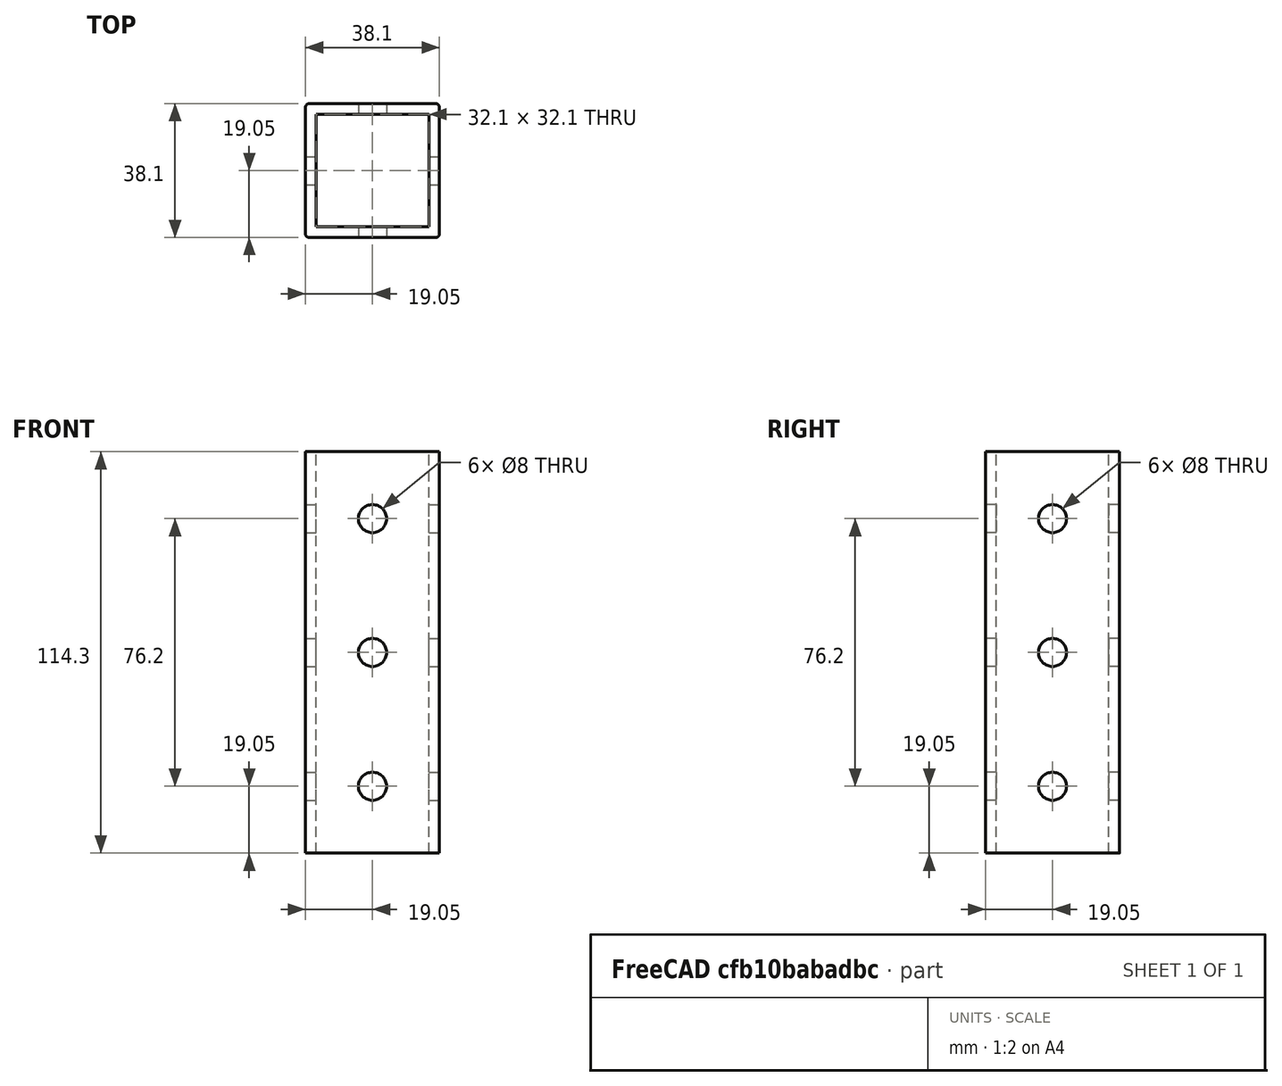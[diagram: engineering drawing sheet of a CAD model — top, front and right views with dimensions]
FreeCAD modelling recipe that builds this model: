
FCSTD DOCUMENT  (FreeCAD 0.15R4671 (Git))
Label: 3x-fillet-hollow
License: All rights reserved
LicenseURL: http://en.wikipedia.org/wiki/All_rights_reserved
objects: Part::Cut×3, Part::Box×2, Part::Cylinder×2, Part::FeaturePython×2, PartDesign::Fillet×1
note: 10 computed .brp shape members not serialized (recipe doc carries the construction recipe); baked Part::Feature solids carry a one-line shape summary decoded from their .brp

FEATURE [Part::Box] Box  label="Beam"
  Height = 114.3
  Length = 38.1
  Width = 38.1
FEATURE [Part::Cylinder] Cylinder
  Angle = 360
  Height = 38.1
  Placement = pos=(0,19.05,19.05) rot=(0,1,0;1.5708rad)
  Radius = 4
FEATURE [Part::Cylinder] Cylinder001
  Angle = 360
  Height = 38.1
  Placement = pos=(19.05,38.1,19.05) rot=(1,0,0;1.5708rad)
  Radius = 4
FEATURE [Part::FeaturePython] Array  label="Holes1"  # Draft array (typed FeaturePython)
  Angle = 360
  ArrayType = 0
  Axis = (0,0,1)
  Base = -> Cylinder001
  Center = (0,0,0)
  Fuse = false
  IntervalAxis = (0,0,0)
  IntervalX = (1,0,0)
  IntervalY = (0,1,0)
  IntervalZ = (0,0,38.1)
  NumberPolar = 1
  NumberX = 1
  NumberY = 1
  NumberZ = 3
FEATURE [Part::FeaturePython] Array001  label="Holes2"  # Draft array (typed FeaturePython)
  Angle = 360
  ArrayType = 0
  Axis = (0,0,1)
  Base = -> Cylinder
  Center = (0,0,0)
  Fuse = false
  IntervalAxis = (0,0,0)
  IntervalX = (1,0,0)
  IntervalY = (0,1,0)
  IntervalZ = (0,0,38.1)
  NumberPolar = 1
  NumberX = 1
  NumberY = 1
  NumberZ = 3
FEATURE [Part::Box] Box001  label="Cutout"
  Height = 114.3
  Length = 32.1
  Placement = pos=(3,3,0) rot=(0,0,1;0rad)
  Width = 32.1
FEATURE [PartDesign::Fillet] Fillet
  Base = -> Box [Edge1,Edge5,Edge7,Edge3]
  Radius = 1
FEATURE [Part::Cut] Cut
  Base = -> Fillet
  Tool = -> Array
FEATURE [Part::Cut] Cut001
  Base = -> Cut
  Tool = -> Array001
FEATURE [Part::Cut] Cut002
  Base = -> Cut001
  Tool = -> Box001
